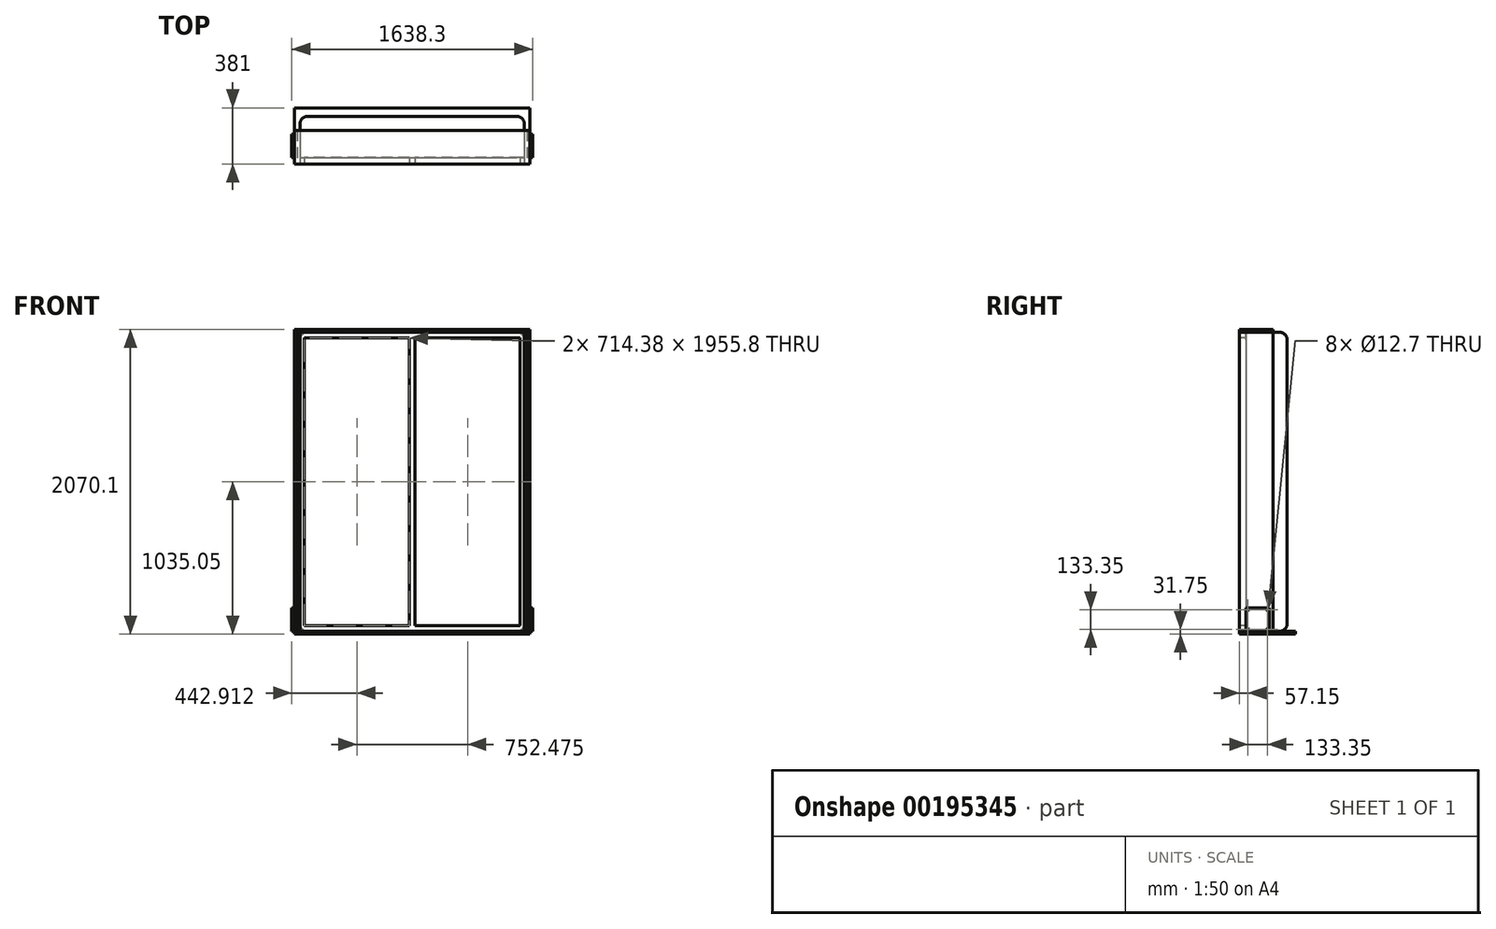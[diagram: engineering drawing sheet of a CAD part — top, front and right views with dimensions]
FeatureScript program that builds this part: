
annotation { "Feature Type Name" : "Feature", "Feature Type Description" : "" }
export const myFeature = defineFeature(function(context is Context, id is Id, definition is map)
    precondition{}
    {
        {
            var Q0;
            Q0=qCreatedBy(makeId("Front.planeOp"),FACE);
            var sketch = newSketch(context, id + "F0", { "sketchPlane" : qUnion([Q0])});
            skLineSegment(sketch, "E0", {"start": v(0, 1359.37) * mm, "end": v(0, -1354.67) * mm, "construction": true});
            skLineSegment(sketch, "E1.bottom", {"start": v(-762, 0) * mm, "end": v(762, 0) * mm});
            skLineSegment(sketch, "E1.top", {"start": v(-762, -2032) * mm, "end": v(762, -2032) * mm});
            skLineSegment(sketch, "E1.left", {"start": v(-762, 0) * mm, "end": v(-762, -2032) * mm});
            skLineSegment(sketch, "E1.right", {"start": v(762, 0) * mm, "end": v(762, -2032) * mm});
            skLineSegment(sketch, "E2", {"start": v(-762, 0) * mm, "end": v(762, -2032) * mm, "construction": true});
            skLineSegment(sketch, "E3", {"start": v(-762, -2032) * mm, "end": v(762, 0) * mm, "construction": true});
            skLineSegment(sketch, "E4.bottom", {"start": v(733.42, -38.1) * mm, "end": v(19.05, -38.1) * mm});
            skLineSegment(sketch, "E4.top", {"start": v(733.43, -1993.9) * mm, "end": v(19.05, -1993.9) * mm});
            skLineSegment(sketch, "E4.left", {"start": v(733.42, -38.1) * mm, "end": v(733.43, -1993.9) * mm});
            skLineSegment(sketch, "E4.right", {"start": v(-733.42, -38.1) * mm, "end": v(-733.42, -1993.9) * mm});
            skPoint(sketch, "E4.middle", {"position": v(0, -1016) * mm});
            skLineSegment(sketch, "E5.left", {"start": v(19.05, -38.1) * mm, "end": v(19.05, -1993.9) * mm});
            skLineSegment(sketch, "E5.right", {"start": v(-19.05, -38.1) * mm, "end": v(-19.05, -1993.9) * mm});
            skLineSegment(sketch, "E6.trimOffspring", {"start": v(-19.05, -1993.9) * mm, "end": v(-733.42, -1993.9) * mm});
            skLineSegment(sketch, "E7.trimOffspring", {"start": v(-19.05, -38.1) * mm, "end": v(-733.42, -38.1) * mm});
            skSolve(sketch);
        }
        {
            var Q0;
            Q0 = qSketchRegion(id + "F0", true);
            extrude(context, id + "F1", {"entities" : qUnion([Q0]), "oppositeDirection" : true, "depth" : 44.45 * mm});
        }
        {
            var Q0;
            Q0=makeQuery(id+"F1.opExtrude","CAP_FACE",FACE,{"disambiguationData":[OSD([sQuery(id+"F0.wireOp",EDGE,"E1.bottom"),sQuery(id+"F0.wireOp",EDGE,"E1.top"),sQuery(id+"F0.wireOp",EDGE,"E1.left"),sQuery(id+"F0.wireOp",EDGE,"E1.right"),sQuery(id+"F0.wireOp",EDGE,"E4.bottom"),sQuery(id+"F0.wireOp",EDGE,"E4.top"),sQuery(id+"F0.wireOp",EDGE,"E4.left"),sQuery(id+"F0.wireOp",EDGE,"E4.right"),sQuery(id+"F0.wireOp",EDGE,"E5.left"),sQuery(id+"F0.wireOp",EDGE,"E5.right"),sQuery(id+"F0.wireOp",EDGE,"E6.trimOffspring"),sQuery(id+"F0.wireOp",EDGE,"E7.trimOffspring")])],"isStart":false});
            var sketch = newSketch(context, id + "F2", { "sketchPlane" : qUnion([Q0])});
            skLineSegment(sketch, "E8.bottom", {"start": v(-762, 0) * mm, "end": v(762, 0) * mm});
            skLineSegment(sketch, "E8.top", {"start": v(-762, -2032) * mm, "end": v(762, -2032) * mm});
            skLineSegment(sketch, "E8.left", {"start": v(-762, 0) * mm, "end": v(-762, -2032) * mm});
            skLineSegment(sketch, "E8.right", {"start": v(762, 0) * mm, "end": v(762, -2032) * mm});
            skSolve(sketch);
        }
        {
            var Q0;
            Q0 = qSketchRegion(id + "F2", true);
            extrude(context, id + "F3", {"entities" : qUnion([Q0]), "depth" : 279.4 * mm});
        }
        {
            var Q0;
            Q0=makeQuery(id+"F3.opExtrude","CAP_FACE",FACE,{"disambiguationData":[OSD([sQuery(id+"F2.wireOp",EDGE,"E8.bottom"),sQuery(id+"F2.wireOp",EDGE,"E8.top"),sQuery(id+"F2.wireOp",EDGE,"E8.left"),sQuery(id+"F2.wireOp",EDGE,"E8.right")])],"isStart":false});
            var Q1;
            Q1=makeQuery(id+"F3.opExtrude","SWEPT_EDGE",EDGE,{"disambiguationData":[OSD([sQuery(id+"F2.wireOp",EDGE,"E8.top"),sQuery(id+"F2.wireOp",EDGE,"E8.right")])]});
            var Q2;
            Q2=makeQuery(id+"F3.opExtrude","SWEPT_EDGE",EDGE,{"disambiguationData":[OSD([sQuery(id+"F2.wireOp",EDGE,"E8.top"),sQuery(id+"F2.wireOp",EDGE,"E8.left")])]});
            var Q3;
            Q3=makeQuery(id+"F3.opExtrude","SWEPT_EDGE",EDGE,{"disambiguationData":[OSD([sQuery(id+"F2.wireOp",EDGE,"E8.bottom"),sQuery(id+"F2.wireOp",EDGE,"E8.left")])]});
            var Q4;
            Q4=makeQuery(id+"F3.opExtrude","SWEPT_EDGE",EDGE,{"disambiguationData":[OSD([sQuery(id+"F2.wireOp",EDGE,"E8.bottom"),sQuery(id+"F2.wireOp",EDGE,"E8.right")])]});
            fillet(context, id + "F4", {"entities" : qUnion([Q0, Q1, Q2, Q3, Q4]), "radius" : 50.8 * mm, "tangentPropagation" : true, "allowEdgeOverflow" : false});
        }
        {
            var Q0;
            Q0=makeQuery(id+"F1.opExtrude","CAP_FACE",FACE,{"disambiguationData":[OSD([sQuery(id+"F0.wireOp",EDGE,"E1.bottom"),sQuery(id+"F0.wireOp",EDGE,"E1.top"),sQuery(id+"F0.wireOp",EDGE,"E1.left"),sQuery(id+"F0.wireOp",EDGE,"E1.right"),sQuery(id+"F0.wireOp",EDGE,"E4.bottom"),sQuery(id+"F0.wireOp",EDGE,"E4.top"),sQuery(id+"F0.wireOp",EDGE,"E4.left"),sQuery(id+"F0.wireOp",EDGE,"E4.right"),sQuery(id+"F0.wireOp",EDGE,"E5.left"),sQuery(id+"F0.wireOp",EDGE,"E5.right"),sQuery(id+"F0.wireOp",EDGE,"E6.trimOffspring"),sQuery(id+"F0.wireOp",EDGE,"E7.trimOffspring")])],"isStart":true});
            var sketch = newSketch(context, id + "F5", { "sketchPlane" : qUnion([Q0])});
            skLineSegment(sketch, "E9.0", {"start": v(-762, -2032) * mm, "end": v(762, -2032) * mm, "construction": true});
            skLineSegment(sketch, "E10", {"start": v(0, 0) * mm, "end": v(0, -2032) * mm, "construction": true});
            skLineSegment(sketch, "E11.bottom", {"start": v(-800.1, -2032) * mm, "end": v(800.1, -2032) * mm});
            skLineSegment(sketch, "E11.top", {"start": v(-800.1, -2051.05) * mm, "end": v(800.1, -2051.05) * mm});
            skLineSegment(sketch, "E11.left", {"start": v(-800.1, -2032) * mm, "end": v(-800.1, -2051.05) * mm});
            skLineSegment(sketch, "E11.right", {"start": v(800.1, -2032) * mm, "end": v(800.1, -2051.05) * mm});
            skSolve(sketch);
        }
        {
            var Q0;
            Q0 = qSketchRegion(id + "F5", true);
            extrude(context, id + "F6", {"entities" : qUnion([Q0]), "oppositeDirection" : true, "depth" : 381 * mm});
        }
        {
            var Q0;
            Q0=makeQuery(id+"F6.opExtrude","CAP_FACE",FACE,{"disambiguationData":[OSD([sQuery(id+"F5.wireOp",EDGE,"E11.bottom"),sQuery(id+"F5.wireOp",EDGE,"E11.top"),sQuery(id+"F5.wireOp",EDGE,"E11.left"),sQuery(id+"F5.wireOp",EDGE,"E11.right")])],"isStart":true});
            var sketch = newSketch(context, id + "F7", { "sketchPlane" : qUnion([Q0])});
            skLineSegment(sketch, "E12.bottom", {"start": v(-800.1, -2032) * mm, "end": v(-781.05, -2032) * mm});
            skLineSegment(sketch, "E12.top", {"start": v(-800.1, 0) * mm, "end": v(-781.05, 0) * mm});
            skLineSegment(sketch, "E12.left", {"start": v(-800.1, -2032) * mm, "end": v(-800.1, 0) * mm});
            skLineSegment(sketch, "E12.right", {"start": v(-781.05, -2032) * mm, "end": v(-781.05, 0) * mm});
            skSolve(sketch);
        }
        {
            var Q0;
            Q0 = qSketchRegion(id + "F7", true);
            extrude(context, id + "F8", {"entities" : qUnion([Q0]), "oppositeDirection" : true, "depth" : 228.6 * mm});
        }
        {
            var Q0;
            Q0=makeQuery(id+"F8.opExtrude","SWEPT_BODY",BODY,{"disambiguationData":[OSD([sQuery(id+"F7.wireOp",EDGE,"E12.bottom"),sQuery(id+"F7.wireOp",EDGE,"E12.top"),sQuery(id+"F7.wireOp",EDGE,"E12.left"),sQuery(id+"F7.wireOp",EDGE,"E12.right")])]});
            var Q1;
            Q1=qCreatedBy(makeId("Right.planeOp"),FACE);
            mirror(context, id + "F9", {"entities" : qUnion([Q0]), "mirrorPlane" : qUnion([Q1])});
        }
        {
            var Q0;
            Q0=makeQuery(id+"F3.opExtrude","CAP_FACE",FACE,{"disambiguationData":[OSD([sQuery(id+"F2.wireOp",EDGE,"E8.bottom"),sQuery(id+"F2.wireOp",EDGE,"E8.top"),sQuery(id+"F2.wireOp",EDGE,"E8.left"),sQuery(id+"F2.wireOp",EDGE,"E8.right")])],"isStart":false});
            cPlane(context, id + "F10", {"entities" : qUnion([Q0]), "cplaneType" : CPlaneType.OFFSET, "offset" : 101.6 * mm, "width" : 152.4 * mm, "height" : 152.4 * mm});
        }
        {
            var Q0;
            Q0=makeQuery(id+"F1.opExtrude","CAP_FACE",FACE,{"disambiguationData":[OSD([sQuery(id+"F0.wireOp",EDGE,"E1.bottom"),sQuery(id+"F0.wireOp",EDGE,"E1.top"),sQuery(id+"F0.wireOp",EDGE,"E1.left"),sQuery(id+"F0.wireOp",EDGE,"E1.right"),sQuery(id+"F0.wireOp",EDGE,"E4.bottom"),sQuery(id+"F0.wireOp",EDGE,"E4.top"),sQuery(id+"F0.wireOp",EDGE,"E4.left"),sQuery(id+"F0.wireOp",EDGE,"E4.right"),sQuery(id+"F0.wireOp",EDGE,"E5.left"),sQuery(id+"F0.wireOp",EDGE,"E5.right"),sQuery(id+"F0.wireOp",EDGE,"E6.trimOffspring"),sQuery(id+"F0.wireOp",EDGE,"E7.trimOffspring")])],"isStart":true});
            var sketch = newSketch(context, id + "F11", { "sketchPlane" : qUnion([Q0])});
            skPoint(sketch, "E13.0", {"position": v(-800.1, 0) * mm});
            skPoint(sketch, "E14.0", {"position": v(800.1, 0) * mm});
            skLineSegment(sketch, "E15.bottom", {"start": v(-800.1, 0) * mm, "end": v(800.1, 0) * mm});
            skLineSegment(sketch, "E15.top", {"start": v(-800.1, 19.05) * mm, "end": v(800.1, 19.05) * mm});
            skLineSegment(sketch, "E15.left", {"start": v(-800.1, 0) * mm, "end": v(-800.1, 19.05) * mm});
            skLineSegment(sketch, "E15.right", {"start": v(800.1, 0) * mm, "end": v(800.1, 19.05) * mm});
            skSolve(sketch);
        }
        {
            var Q0;
            Q0 = qSketchRegion(id + "F11", true);
            var Q1;
            Q1=makeQuery(id+"F8.opExtrude","CAP_FACE",FACE,{"disambiguationData":[OSD([sQuery(id+"F7.wireOp",EDGE,"E12.bottom"),sQuery(id+"F7.wireOp",EDGE,"E12.top"),sQuery(id+"F7.wireOp",EDGE,"E12.left"),sQuery(id+"F7.wireOp",EDGE,"E12.right")])],"isStart":false});
            extrude(context, id + "F12", {"entities" : qUnion([Q0]), "endBound" : BoundingType.UP_TO_SURFACE, "oppositeDirection" : true, "endBoundEntityFace" : qUnion([Q1]), "depth" : 25.4 * mm});
        }
        {
            var Q0;
            Q0=makeQuery(id+"F8.opExtrude","SWEPT_FACE",FACE,{"disambiguationData":[OSD([sQuery(id+"F7.wireOp",EDGE,"E12.left")])]});
            var sketch = newSketch(context, id + "F13", { "sketchPlane" : qUnion([Q0])});
            skLineSegment(sketch, "E16.bottom", {"start": v(-44.45, -2032) * mm, "end": v(-203.2, -2032) * mm});
            skLineSegment(sketch, "E16.top", {"start": v(-44.45, -1873.25) * mm, "end": v(-203.2, -1873.25) * mm});
            skLineSegment(sketch, "E16.left", {"start": v(-44.45, -2032) * mm, "end": v(-44.45, -1873.25) * mm});
            skLineSegment(sketch, "E16.right", {"start": v(-203.2, -2032) * mm, "end": v(-203.2, -1873.25) * mm});
            skLineSegment(sketch, "E17", {"start": v(-203.2, -1873.25) * mm, "end": v(-44.45, -2032) * mm, "construction": true});
            skLineSegment(sketch, "E18", {"start": v(-123.83, -1873.25) * mm, "end": v(-123.82, -2032) * mm, "construction": true});
            skLineSegment(sketch, "E19", {"start": v(-203.2, -1952.62) * mm, "end": v(-44.45, -1952.62) * mm, "construction": true});
            skCircle(sketch, "E20", {"center": v(-57.15, -1885.95) * mm, "radius": 6.35 * mm});
            skCircle(sketch, "E21.MirrorC", {"center": v(-190.5, -1885.95) * mm, "radius": 6.35 * mm});
            skCircle(sketch, "E22.MirrorC", {"center": v(-190.5, -2019.3) * mm, "radius": 6.35 * mm});
            skCircle(sketch, "E23.MirrorC", {"center": v(-57.15, -2019.3) * mm, "radius": 6.35 * mm});
            skPoint(sketch, "E24", {"position": v(-123.82, -1952.62) * mm});
            skCircle(sketch, "E25", {"center": v(-123.82, -1952.62) * mm, "radius": 301.63 * mm, "construction": true});
            skLineSegment(sketch, "E26", {"start": v(-425.45, -1306.75) * mm, "end": v(-425.45, -1952.62) * mm, "construction": true});
            skCircle(sketch, "E27", {"center": v(-123.82, -1952.62) * mm, "radius": 275.37 * mm, "construction": true});
            skSolve(sketch);
        }
        {
            var Q0;
            Q0 = qSketchRegion(id + "F13", true);
            extrude(context, id + "F14", {"entities" : qUnion([Q0]), "depth" : 19.05 * mm});
        }
        {
            var Q0;
            Q0=makeQuery(id+"F14.opExtrude","SWEPT_BODY",BODY,{"disambiguationData":[OSD([sQuery(id+"F13.wireOp",EDGE,"E16.bottom"),sQuery(id+"F13.wireOp",EDGE,"E16.top"),sQuery(id+"F13.wireOp",EDGE,"E16.left"),sQuery(id+"F13.wireOp",EDGE,"E16.right"),sQuery(id+"F13.wireOp",EDGE,"E20"),sQuery(id+"F13.wireOp",EDGE,"E21.MirrorC"),sQuery(id+"F13.wireOp",EDGE,"E22.MirrorC"),sQuery(id+"F13.wireOp",EDGE,"E23.MirrorC")])]});
            var Q1;
            Q1=qCreatedBy(makeId("Right.planeOp"),FACE);
            mirror(context, id + "F15", {"entities" : qUnion([Q0]), "mirrorPlane" : qUnion([Q1])});
        }
    });
